# Revit family: Towel_Bar-American_Standard-Townsend-73530XX_Series
name_source: partatom
category: Specialty Equipment
units: mm (PartAtom-declared; Revit-internal decimal feet)

## family parameters
Cut with Voids When Loaded = No
Host = Face
OmniClass Number = 23.40.20.21.27
OmniClass Title = Towel Bars
Part Type = Normal
Room Calculation Point = No
Round Connector Dimension = Use Diameter
Shared = Yes

## types (10) — shared parameters
Assembly Code = C1030220
Default Elevation = 48"
Height = 2 1/4"
Installation Instruction Link = https://lixil.cdn.celum.cloud
Installation Type = Wall Mount
Manufacturer = American Standard
Price = Prices may vary. Please consult Manufacturer Representative for most up-to-date price list.
Product Documentation Link = https://lixil.cdn.celum.cloud
Product Page URL = https://www.americanstandard-us.com
Revised Date = 02/20/2024
URL = https://www.americanstandard-us.com
Warranty Information = Lifetime Warranty
Width = 4"

## per-type parameters (varying)
| type | Description | Finish | Length | Material |
| 7353018.002 | Townsend® 18-Inch Towel Bar | Metal-American Standard-002-Polished Chrome | 18" | Metal-American Standard-002-Polished Chrome |
| 7353024.002 | Townsend® 24-Inch Towel Bar | Metal-American Standard-002-Polished Chrome | 24" | Metal-American Standard-002-Polished Chrome |
| 7353018.013 | Townsend® 18-Inch Towel Bar | Metal-American Standard-013-Polished Nickel | 18" | Metal-American Standard-013-Polished Nickel |
| 7353018.295 | Townsend® 18-Inch Towel Bar | Metal-American Standard-295-PVD Satin Nickel | 18" | Metal-American Standard-295-PVD Satin Nickel |
| 7353024.013 | Townsend® 24-Inch Towel Bar | Metal-American Standard-013-Polished Nickel | 24" | Metal-American Standard-013-Polished Nickel |
| 7353024.295 | Townsend® 24-Inch Towel Bar | Metal-American Standard-295-PVD Satin Nickel | 24" | Metal-American Standard-295-PVD Satin Nickel |
| 7353018.GN0 | Townsend® 18-Inch Towel Bar | Metal-American Standard-GN0-Brushed Cool Sunrise | 18" | Metal-American Standard-GN0-Brushed Cool Sunrise |
| 7353024.GN0 | Townsend® 24-Inch Towel Bar | Metal-American Standard-GN0-Brushed Cool Sunrise | 24" | Metal-American Standard-GN0-Brushed Cool Sunrise |
| 7353024.243 | Townsend® 24-Inch Towel Bar | Metal-American Standard-243-Matte Black | 24" | Metal-American Standard-243-Matte Black |
| 7353018.243 | Townsend® 18-Inch Towel Bar | Metal-American Standard-243-Matte Black | 18" | Metal-American Standard-243-Matte Black |

note: column(s) folded — value = type name in every type: Model

## geometry (parser evidence)
native form markers: Sweep x3
no freeform markers — native parametric forms only
